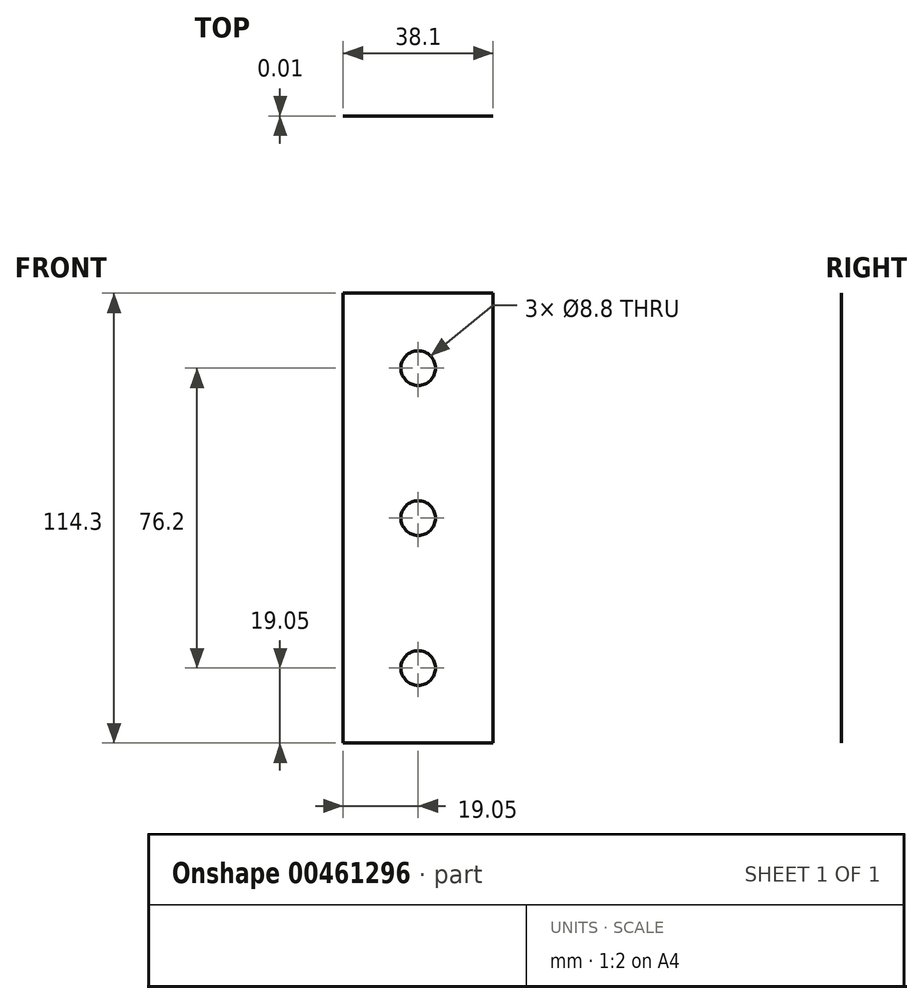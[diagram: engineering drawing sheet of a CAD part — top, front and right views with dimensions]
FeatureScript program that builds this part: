
annotation { "Feature Type Name" : "Feature", "Feature Type Description" : "" }
export const myFeature = defineFeature(function(context is Context, id is Id, definition is map)
    precondition{}
    {
        {
            var Q0;
            Q0=qCreatedBy(makeId("Front.planeOp"),FACE);
            var sketch = newSketch(context, id + "F0", { "sketchPlane" : qUnion([Q0])});
            skLineSegment(sketch, "E0", {"start": v(0, 0) * mm, "end": v(0, 114.3) * mm});
            skLineSegment(sketch, "E1", {"start": v(0, 114.3) * mm, "end": v(38.1, 114.3) * mm});
            skLineSegment(sketch, "E2", {"start": v(38.1, 114.3) * mm, "end": v(38.1, 0) * mm});
            skLineSegment(sketch, "E3", {"start": v(38.1, 0) * mm, "end": v(0, 0) * mm});
            skPoint(sketch, "E4", {"position": v(19.05, 95.25) * mm});
            skPoint(sketch, "E5", {"position": v(19.05, 57.15) * mm});
            skPoint(sketch, "E6", {"position": v(19.05, 19.05) * mm});
            skSolve(sketch);
        }
        {
            var Q0;
            Q0=qSketchRegion(id+"F0",true);
            extrude(context, id + "F1", {"entities" : qUnion([Q0]), "oppositeDirection" : true, "depth" : 1 / 101.6 * mm, "offsetDistance" : 25 * mm});
        }
        {
            var Q0;
            Q0=sQuery(id+"F0.wireOp",VERTEX,"E4");
            var Q1;
            Q1=sQuery(id+"F0.wireOp",VERTEX,"E5");
            var Q2;
            Q2=sQuery(id+"F0.wireOp",VERTEX,"E6");
            var Q3;
            Q3=sQuery(id+"F0.wireOp",VERTEX,"190b6440-769a-4f98-be16-85b98244e9e3");
            var Q4;
            Q4=sQuery(id+"F0.wireOp",VERTEX,"7eecf8ea-fb0a-4127-a916-d15a6602453e");
            var Q5;
            Q5=makeQuery(id+"F1.opExtrude","SWEPT_BODY",BODY,{"disambiguationData":[OSD([sQuery(id+"F0.wireOp",EDGE,"E0"),sQuery(id+"F0.wireOp",EDGE,"E1"),sQuery(id+"F0.wireOp",EDGE,"E2"),sQuery(id+"F0.wireOp",EDGE,"1eDsCvDh-7bzL-5sCi-Albj-Uqkx6I4Ab1Y7"),sQuery(id+"F0.wireOp",EDGE,"uJklmBSJ-NmNr-B2uL-47Tt-p8A2vM7omcX7"),sQuery(id+"F0.wireOp",EDGE,"E3")])]});
            hole(context, id + "F2", {"style" : HoleStyle.SIMPLE, "endStyle" : HoleEndStyle.THROUGH, "standardTappedOrClearance" : lookupTablePath({ "standard" : "ISO", "fit" : "Normal", "size" : "M8", "type" : "Clearance" }), "standardBlindInLast" : lookupTablePath({ "fit" : "Standard", "standard" : "ISO", "size" : "M8", "type" : "Clearance" }), "holeDiameter" : 8.8 * mm, "majorDiameter" : 16 * mm, "isTappedThrough" : true, "tappedDepth" : 12 * mm, "tapClearance" : 3, "locations" : qUnion([Q0, Q1, Q2, Q3, Q4]), "scope" : qUnion([Q5])});
        }
    });
